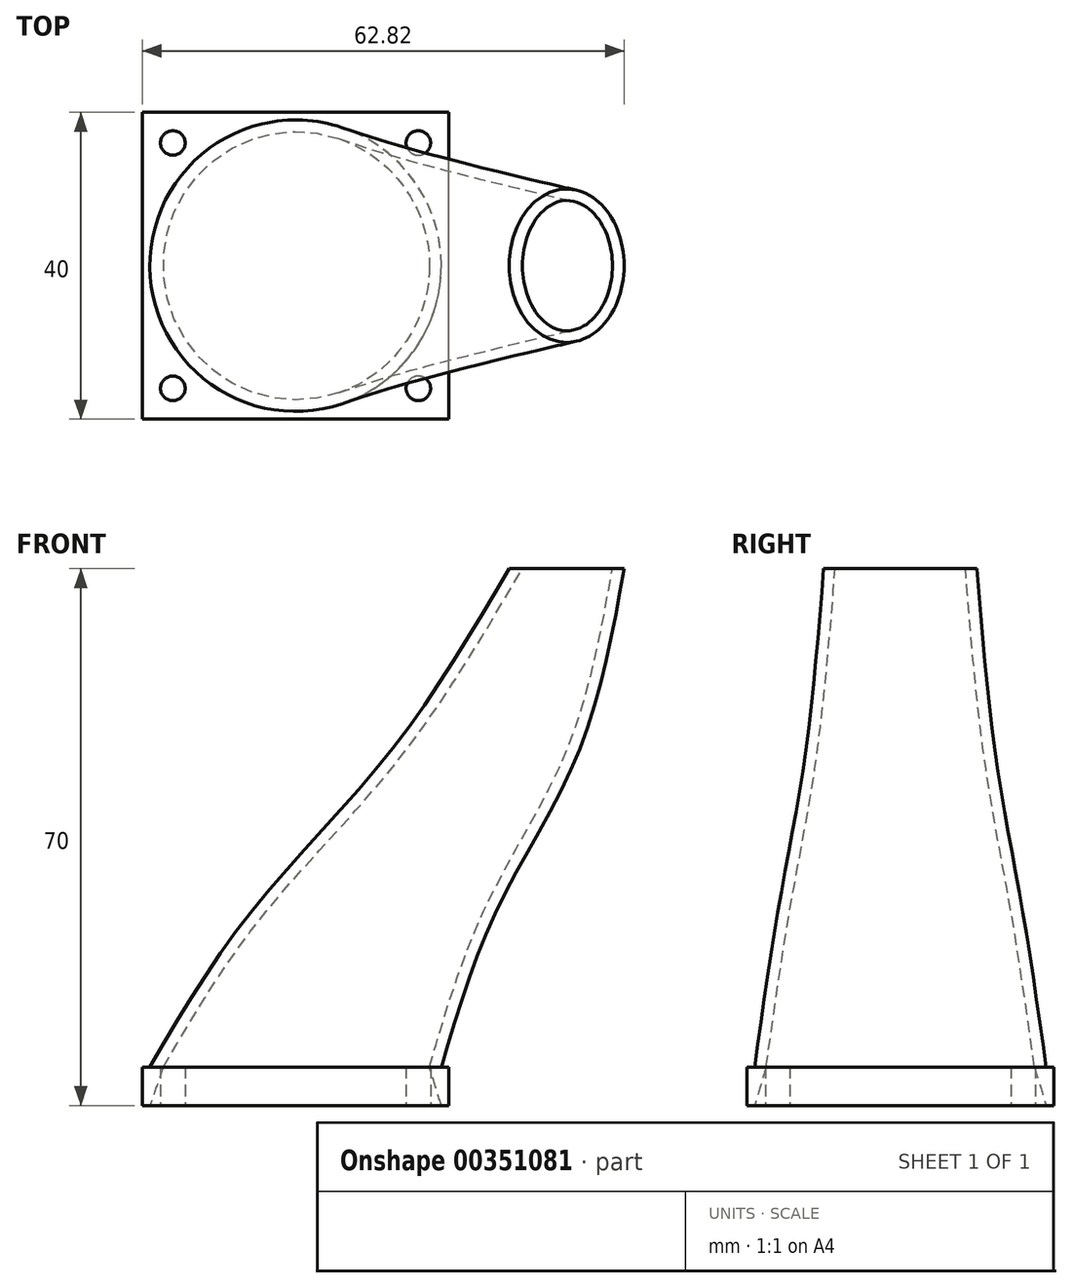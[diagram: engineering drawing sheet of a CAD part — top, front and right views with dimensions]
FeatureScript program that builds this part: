
annotation { "Feature Type Name" : "Feature", "Feature Type Description" : "" }
export const myFeature = defineFeature(function(context is Context, id is Id, definition is map)
    precondition{}
    {
        {
            var Q0;
            Q0=qCreatedBy(makeId("Top.planeOp"),FACE);
            var sketch = newSketch(context, id + "F0", { "sketchPlane" : qUnion([Q0])});
            skCircle(sketch, "E0", {"center": v(0, 0) * mm, "radius": 19 * mm});
            skLineSegment(sketch, "E1.bottom", {"start": v(-20, -20) * mm, "end": v(20, -20) * mm});
            skLineSegment(sketch, "E1.top", {"start": v(-20, 20) * mm, "end": v(20, 20) * mm});
            skLineSegment(sketch, "E1.left", {"start": v(-20, -20) * mm, "end": v(-20, 20) * mm});
            skLineSegment(sketch, "E1.right", {"start": v(20, -20) * mm, "end": v(20, 20) * mm});
            skCircle(sketch, "E2", {"center": v(-16, 16) * mm, "radius": 1.6 * mm});
            skCircle(sketch, "E3", {"center": v(-16, -16) * mm, "radius": 1.6 * mm});
            skCircle(sketch, "E4", {"center": v(16, -16) * mm, "radius": 1.6 * mm});
            skCircle(sketch, "E5", {"center": v(16, 16) * mm, "radius": 1.6 * mm});
            skSolve(sketch);
        }
        {
            var Q0;
            Q0=qCreatedBy(makeId("Top.planeOp"),FACE);
            cPlane(context, id + "F1", {"entities" : qUnion([Q0]), "cplaneType" : CPlaneType.OFFSET, "offset" : 5 * mm, "width" : 150 * mm, "height" : 150 * mm});
        }
        {
            var Q0;
            Q0=qCreatedBy(id+"F1.planeOp",FACE);
            var sketch = newSketch(context, id + "F2", { "sketchPlane" : qUnion([Q0])});
            skCircle(sketch, "E6", {"center": v(0, 0) * mm, "radius": 19 * mm});
            skSolve(sketch);
        }
        {
            var Q0;
            Q0=qCreatedBy(makeId("Top.planeOp"),FACE);
            cPlane(context, id + "F3", {"entities" : qUnion([Q0]), "cplaneType" : CPlaneType.OFFSET, "offset" : 25 * mm, "width" : 150 * mm, "height" : 150 * mm});
        }
        {
            var Q0;
            Q0=qCreatedBy(id+"F3.planeOp",FACE);
            var sketch = newSketch(context, id + "F4", { "sketchPlane" : qUnion([Q0])});
            skCircle(sketch, "E7", {"center": v(10, 0) * mm, "radius": 16 * mm});
            skSolve(sketch);
        }
        {
            var Q0;
            Q0=qCreatedBy(id+"F3.planeOp",FACE);
            cPlane(context, id + "F5", {"entities" : qUnion([Q0]), "cplaneType" : CPlaneType.OFFSET, "offset" : 20 * mm, "width" : 150 * mm, "height" : 150 * mm});
        }
        {
            var Q0;
            Q0=qCreatedBy(id+"F5.planeOp",FACE);
            var sketch = newSketch(context, id + "F6", { "sketchPlane" : qUnion([Q0])});
            skPoint(sketch, "E8.middle", {"position": v(23.93, 0) * mm});
            skCircle(sketch, "E9", {"center": v(23.93, 0) * mm, "radius": 12.5 * mm});
            skSolve(sketch);
        }
        {
            var Q0;
            Q0=qCreatedBy(id+"F5.planeOp",FACE);
            cPlane(context, id + "F7", {"entities" : qUnion([Q0]), "cplaneType" : CPlaneType.OFFSET, "offset" : 25 * mm, "width" : 150 * mm, "height" : 150 * mm});
        }
        {
            var Q0;
            Q0=qCreatedBy(id+"F7.planeOp",FACE);
            var sketch = newSketch(context, id + "F8", { "sketchPlane" : qUnion([Q0])});
            skEllipse(sketch, "E10", {"center": v(35.32, 0) * mm, "majorRadius": 10 * mm, "minorRadius": 7.5 * mm, "majorAxis": v(0, 1)});
            skSolve(sketch);
        }
        {
            var Q0;
            Q0=makeQuery(id+"F2.imprint","IMPRINT",FACE,{"disambiguationData":[TD([[makeQuery(id+"F2.imprint","IMPRINT",EDGE,{"derivedFrom":sQuery(id+"F2.wireOp",EDGE,"E6")}),1.0]])]});
            var Q1;
            Q1=makeQuery(id+"F4.imprint","IMPRINT",FACE,{"disambiguationData":[TD([[makeQuery(id+"F4.imprint","IMPRINT",EDGE,{"derivedFrom":sQuery(id+"F4.wireOp",EDGE,"E7")}),1.0]])]});
            var Q2;
            Q2=makeQuery(id+"F6.imprint","IMPRINT",FACE,{"disambiguationData":[TD([[makeQuery(id+"F6.imprint","IMPRINT",EDGE,{"derivedFrom":sQuery(id+"F6.wireOp",EDGE,"E9")}),1.0]])]});
            var Q3;
            Q3=makeQuery(id+"F8.imprint","IMPRINT",FACE,{"disambiguationData":[TD([[makeQuery(id+"F8.imprint","IMPRINT",EDGE,{"derivedFrom":sQuery(id+"F8.wireOp",EDGE,"E10")}),1.0]])]});
            loft(context, id + "F9", {"sheetProfilesArray" : [{ "sheetProfileEntities" : qUnion([Q0]) }, { "sheetProfileEntities" : qUnion([Q1]) }, { "sheetProfileEntities" : qUnion([Q2]) }, { "sheetProfileEntities" : qUnion([Q3]) }]});
        }
        {
            var Q0;
            Q0=makeQuery(id+"F9.opLoft","CAP_FACE",FACE,{"disambiguationData":[OSD([makeQuery(id+"F2.imprint","IMPRINT",FACE,{"disambiguationData":[TD([[makeQuery(id+"F2.imprint","IMPRINT",EDGE,{"derivedFrom":sQuery(id+"F2.wireOp",EDGE,"E6")}),1.0]])]})])],"isStart":true});
            extrude(context, id + "F10", {"entities" : qUnion([Q0]), "operationType" : NewBodyOperationType.ADD, "depth" : 5 * mm});
        }
        {
            var Q0;
            Q0=makeQuery(id+"F0.imprint","IMPRINT",FACE,{"disambiguationData":[TD([[makeQuery(id+"F0.imprint","IMPRINT",EDGE,{"derivedFrom":sQuery(id+"F0.wireOp",EDGE,"E0")}),-1.0]])]});
            extrude(context, id + "F11", {"entities" : qUnion([Q0]), "operationType" : NewBodyOperationType.ADD, "depth" : 5 * mm});
        }
        {
            var Q0;
            Q0=makeQuery(id+"F9.opLoft","CAP_FACE",FACE,{"disambiguationData":[OSD([makeQuery(id+"F4.imprint","IMPRINT",FACE,{"disambiguationData":[TD([[makeQuery(id+"F4.imprint","IMPRINT",EDGE,{"derivedFrom":sQuery(id+"F4.wireOp",EDGE,"E7")}),1.0]])]})])],"isStart":true});
            var Q1;
            Q1=makeQuery(id+"F9.opLoft","CAP_FACE",FACE,{"disambiguationData":[OSD([makeQuery(id+"F8.imprint","IMPRINT",FACE,{"disambiguationData":[TD([[makeQuery(id+"F8.imprint","IMPRINT",EDGE,{"derivedFrom":sQuery(id+"F8.wireOp",EDGE,"E10")}),1.0]])]})])],"isStart":true});
            shell(context, id + "F12", {"entities" : qUnion([Q0, Q1]), "thickness" : 1.5 * mm});
        }
        {
            var Q0;
            Q0=makeQuery(id+"F12.opShell","OFFSET_FACE",FACE,{"disambiguationData":[OSD([sQuery(id+"F0.wireOp",EDGE,"E0"),sQuery(id+"F0.wireOp",EDGE,"E1.bottom"),sQuery(id+"F0.wireOp",EDGE,"E1.top"),sQuery(id+"F0.wireOp",EDGE,"E1.left"),sQuery(id+"F0.wireOp",EDGE,"E1.right"),sQuery(id+"F0.wireOp",EDGE,"E2"),sQuery(id+"F0.wireOp",EDGE,"E3"),sQuery(id+"F0.wireOp",EDGE,"E4"),sQuery(id+"F0.wireOp",EDGE,"E5"),makeQuery(id+"F2.imprint","IMPRINT",FACE,{"disambiguationData":[TD([[makeQuery(id+"F2.imprint","IMPRINT",EDGE,{"derivedFrom":sQuery(id+"F2.wireOp",EDGE,"E6")}),1.0]])]})])]});
            extrude(context, id + "F13", {"entities" : qUnion([Q0]), "operationType" : NewBodyOperationType.ADD, "depth" : 3.5 * mm});
        }
        {
            var Q1;
            Q1=makeQuery(id+"F0.imprint","IMPRINT",FACE,{"disambiguationData":[TD([[makeQuery(id+"F0.imprint","IMPRINT",EDGE,{"derivedFrom":sQuery(id+"F0.wireOp",EDGE,"E0")}),1.0]])]});
            var Q2;
            Q2=makeQuery(id+"F13.opExtrude","CAP_FACE",FACE,{"disambiguationData":[OSD([sQuery(id+"F0.wireOp",EDGE,"E0"),sQuery(id+"F0.wireOp",EDGE,"E1.bottom"),sQuery(id+"F0.wireOp",EDGE,"E1.top"),sQuery(id+"F0.wireOp",EDGE,"E1.left"),sQuery(id+"F0.wireOp",EDGE,"E1.right"),sQuery(id+"F0.wireOp",EDGE,"E2"),sQuery(id+"F0.wireOp",EDGE,"E3"),sQuery(id+"F0.wireOp",EDGE,"E4"),sQuery(id+"F0.wireOp",EDGE,"E5"),makeQuery(id+"F2.imprint","IMPRINT",FACE,{"disambiguationData":[TD([[makeQuery(id+"F2.imprint","IMPRINT",EDGE,{"derivedFrom":sQuery(id+"F2.wireOp",EDGE,"E6")}),1.0]])]})])],"isStart":false});
            loft(context, id + "F14", {"operationType" : NewBodyOperationType.REMOVE, "sheetProfilesArray" : [{ "sheetProfileEntities" : qUnion([Q1]) }, { "sheetProfileEntities" : qUnion([Q2]) }]});
        }
    });
